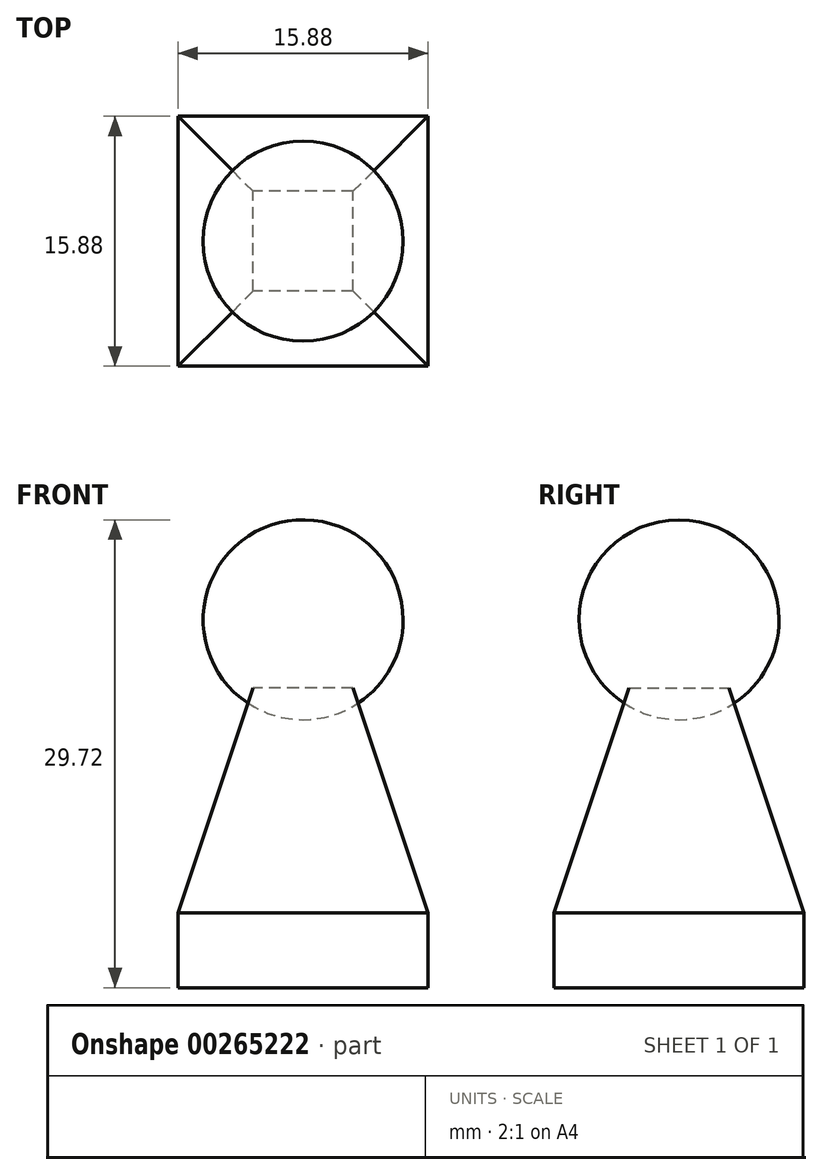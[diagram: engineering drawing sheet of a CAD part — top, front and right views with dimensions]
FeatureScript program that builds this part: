
annotation { "Feature Type Name" : "Feature", "Feature Type Description" : "" }
export const myFeature = defineFeature(function(context is Context, id is Id, definition is map)
    precondition{}
    {
        {
            var Q0;
            Q0=qCreatedBy(makeId("Top.planeOp"),FACE);
            var sketch = newSketch(context, id + "F0", { "sketchPlane" : qUnion([Q0])});
            skLineSegment(sketch, "E0.bottom", {"start": v(7.94, -7.94) * mm, "end": v(-7.94, -7.94) * mm});
            skLineSegment(sketch, "E0.top", {"start": v(7.94, 7.94) * mm, "end": v(-7.94, 7.94) * mm});
            skLineSegment(sketch, "E0.left", {"start": v(7.94, -7.94) * mm, "end": v(7.94, 7.94) * mm});
            skLineSegment(sketch, "E0.right", {"start": v(-7.94, -7.94) * mm, "end": v(-7.94, 7.94) * mm});
            skPoint(sketch, "E0.middle", {"position": v(0, 0) * mm});
            skSolve(sketch);
        }
        {
            var Q0;
            Q0 = qSketchRegion(id + "F0", true);
            extrude(context, id + "F1", {"entities" : qUnion([Q0]), "depth" : 4.76 * mm});
        }
        {
            var Q0;
            Q0=makeQuery(id+"F1.opExtrude","CAP_FACE",FACE,{"disambiguationData":[OSD([sQuery(id+"F0.wireOp",EDGE,"E0.bottom"),sQuery(id+"F0.wireOp",EDGE,"E0.top"),sQuery(id+"F0.wireOp",EDGE,"E0.left"),sQuery(id+"F0.wireOp",EDGE,"E0.right")])],"isStart":false});
            cPlane(context, id + "F2", {"entities" : qUnion([Q0]), "cplaneType" : CPlaneType.OFFSET, "offset" : 14.29 * mm, "width" : 152.4 * mm, "height" : 152.4 * mm});
        }
        {
            var Q0;
            Q0=qCreatedBy(id+"F2.planeOp",FACE);
            var sketch = newSketch(context, id + "F3", { "sketchPlane" : qUnion([Q0])});
            skLineSegment(sketch, "E1.bottom", {"start": v(3.18, -3.17) * mm, "end": v(-3.18, -3.18) * mm});
            skLineSegment(sketch, "E1.top", {"start": v(3.18, 3.18) * mm, "end": v(-3.18, 3.17) * mm});
            skLineSegment(sketch, "E1.left", {"start": v(3.18, -3.17) * mm, "end": v(3.18, 3.18) * mm});
            skLineSegment(sketch, "E1.right", {"start": v(-3.18, -3.18) * mm, "end": v(-3.18, 3.17) * mm});
            skPoint(sketch, "E1.middle", {"position": v(0, 0) * mm});
            skSolve(sketch);
        }
        {
            var Q1;
            Q1=makeQuery(id+"F1.opExtrude","CAP_FACE",FACE,{"disambiguationData":[OSD([sQuery(id+"F0.wireOp",EDGE,"E0.bottom"),sQuery(id+"F0.wireOp",EDGE,"E0.top"),sQuery(id+"F0.wireOp",EDGE,"E0.left"),sQuery(id+"F0.wireOp",EDGE,"E0.right")])],"isStart":false});
            var Q2;
            Q2 = qSketchRegion(id + "F3", true);
            loft(context, id + "F4", {"operationType" : NewBodyOperationType.ADD, "sheetProfilesArray" : [{ "sheetProfileEntities" : qUnion([Q1]) }, { "sheetProfileEntities" : qUnion([Q2]) }]});
        }
        {
            var Q0;
            Q0=qCreatedBy(id+"F2.planeOp",FACE);
            cPlane(context, id + "F5", {"entities" : qUnion([Q0]), "cplaneType" : CPlaneType.OFFSET, "offset" : 4.32 * mm, "width" : 152.4 * mm, "height" : 152.4 * mm});
        }
        {
            var Q0;
            Q0=qCreatedBy(id+"F5.planeOp",FACE);
            var sketch = newSketch(context, id + "F6", { "sketchPlane" : qUnion([Q0])});
            skArc(sketch, "E2", {"start": v(0, 6.35) * mm, "mid": v(-6.35, 0) * mm, "end": v(0, -6.35) * mm});
            skLineSegment(sketch, "E3", {"start": v(0, 6.35) * mm, "end": v(0, -6.35) * mm});
            skSolve(sketch);
        }
        {
            var Q0;
            Q0=makeQuery(id+"F6.imprint","IMPRINT",FACE,{"disambiguationData":[TD([[makeQuery(id+"F6.imprint","IMPRINT",EDGE,{"derivedFrom":sQuery(id+"F6.wireOp",EDGE,"E2")}),1.0]])]});
            var Q1;
            Q1=sQuery(id+"F6.wireOp",EDGE,"E3");
            revolve(context, id + "F7", {"entities" : qUnion([Q0]), "axis" : qUnion([Q1]), "revolveType" : RevolveType.FULL});
        }
    });
